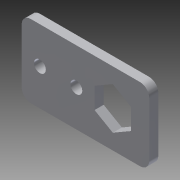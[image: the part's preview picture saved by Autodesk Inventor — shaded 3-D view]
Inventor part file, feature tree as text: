
AUTODESK INVENTOR PART (.ipt)
format: ipt  version: 2014 (Build 180170000, 170)  size: 100,352 bytes
history: native  units: in
note: dims shown in document units (in); Inventor stores cm internally (conversion verified against a paired STEP export)
features: extrude x1, fillet x1, sketch x1
ambient origin geometry x8: Origin, YZ Plane, XZ Plane, XY Plane, X Axis, Y Axis, Z Axis, Center Point
bodies: Solid1 (feature_tree)
feature tree (3):
  extrude  "Extrusion1"  Depth=1.0in
  fillet  "Fillet1"  Radius=0.163in
  sketch  "Sketch1"  dims[d0=1.75in d1=1.0in d2=0.163in d3=0.5in d4=0.25in d5=1.0in d6=0.5in d7=0.5in d8=0.125in d9=0.0in d10=0.125in d11=0.7874in d13=0.5in d14=0.3937in d16=1.0in]
